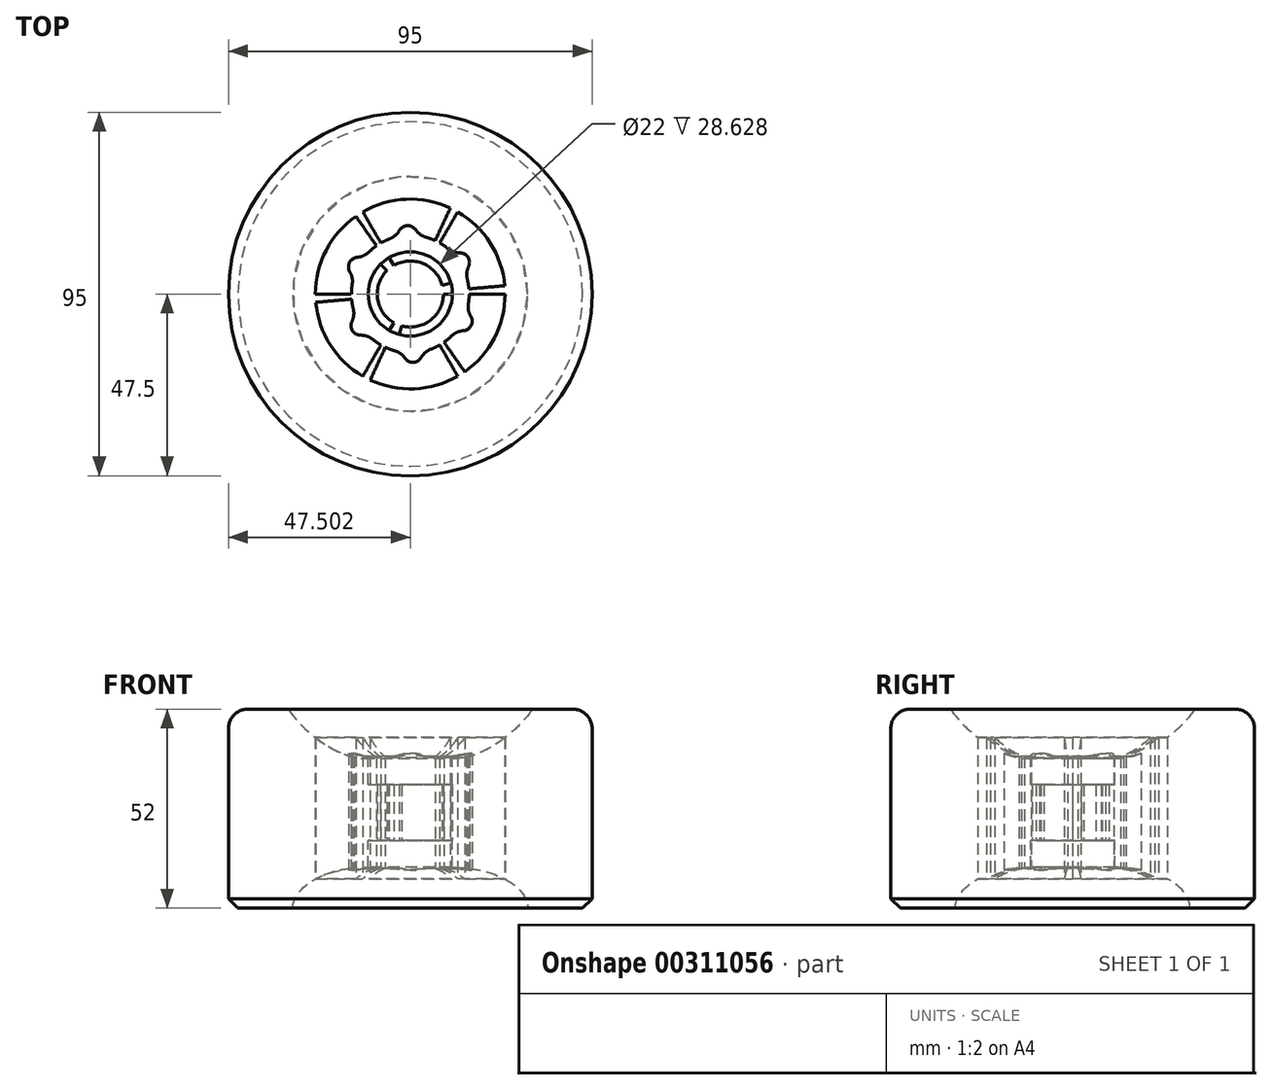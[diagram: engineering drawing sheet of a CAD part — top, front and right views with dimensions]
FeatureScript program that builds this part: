
annotation { "Feature Type Name" : "Feature", "Feature Type Description" : "" }
export const myFeature = defineFeature(function(context is Context, id is Id, definition is map)
    precondition{}
    {
        {
            var Q0;
            Q0=qCreatedBy(makeId("Front.planeOp"),FACE);
            var sketch = newSketch(context, id + "F0", { "sketchPlane" : qUnion([Q0])});
            skLineSegment(sketch, "E0", {"start": v(-20.2, 7.77) * mm, "end": v(-4.58, 7.77) * mm});
            skLineSegment(sketch, "E1", {"start": v(-20.2, 7.77) * mm, "end": v(-20.2, -18.23) * mm});
            skLineSegment(sketch, "E2", {"start": v(27.3, 7.77) * mm, "end": v(27.3, -18.23) * mm, "construction": true});
            skLineSegment(sketch, "E3", {"start": v(-20.2, -18.23) * mm, "end": v(-20.2, -44.23) * mm});
            skLineSegment(sketch, "E4", {"start": v(-20.2, -44.23) * mm, "end": v(-3.37, -44.23) * mm});
            skLineSegment(sketch, "E5", {"start": v(27.3, -18.23) * mm, "end": v(27.3, -44.23) * mm, "construction": true});
            skLineSegment(sketch, "E6", {"start": v(16.3, -4.93) * mm, "end": v(16.3, -33.56) * mm});
            skEllipticalArc(sketch, "E7", {});
            skEllipticalArc(sketch, "E8", {});
            const initialGuessF0  = {"E7": [0.006164850201457739, 0.0077684287428855915, -0.7508845168032906, 0.6604335261213568, 0.017096453369235928, 0.008044444951375029, 1.0795611750690233, 2.780946730637043], "E8": [0.016301685365613657, -0.04423157125711441, -1, 0, 0.01967554039205249, 0.010675819649360317, 4.71238898038469, 0]};
            skSetInitialGuess(sketch, initialGuessF0);
            skSolve(sketch);
        }
        {
            var Q0;
            Q0 = qSketchRegion(id + "F0", true);
            var Q1;
            Q1=sQuery(id+"F0.wireOp",EDGE,"E5");
            revolve(context, id + "F1", {"entities" : qUnion([Q0]), "axis" : qUnion([Q1]), "revolveType" : RevolveType.FULL});
        }
        {
            var Q0;
            Q0=makeQuery(id+"F1.opRevolve","SWEPT_EDGE",EDGE,{"disambiguationData":[OSD([sQuery(id+"F0.wireOp",EDGE,"E0"),sQuery(id+"F0.wireOp",EDGE,"E1")])]});
            fillet(context, id + "F2", {"entities" : qUnion([Q0]), "radius" : 5 * mm, "tangentPropagation" : true, "allowEdgeOverflow" : false});
        }
        {
            var Q0;
            Q0=makeQuery(id+"F1.opRevolve","SWEPT_EDGE",EDGE,{"disambiguationData":[OSD([sQuery(id+"F0.wireOp",EDGE,"E0"),sQuery(id+"F0.wireOp",EDGE,"E7")])]});
            fillet(context, id + "F3", {"entities" : qUnion([Q0]), "radius" : 1 * mm, "tangentPropagation" : true, "allowEdgeOverflow" : false});
        }
        {
            var Q0;
            Q0=makeQuery(id+"F1.opRevolve","SWEPT_FACE",FACE,{"disambiguationData":[OSD([sQuery(id+"F0.wireOp",EDGE,"E4")])]});
            var sketch = newSketch(context, id + "F4", { "sketchPlane" : qUnion([Q0])});
            skPoint(sketch, "E9.center", {"position": v(27.3, 0) * mm});
            skLineSegment(sketch, "E10.2.0", {"start": v(39.7, 21.46) * mm, "end": v(35, 13.32) * mm});
            skLineSegment(sketch, "E11.2.0", {"start": v(16.83, 22.46) * mm, "end": v(20.8, 13.94) * mm});
            skArc(sketch, "E12.trimOffspring", {"start": v(35, 13.32) * mm, "mid": v(33.88, 13.9) * mm, "end": v(32.73, 14.4) * mm});
            skArc(sketch, "E13.trimOffspring", {"start": v(39.7, 21.46) * mm, "mid": v(28.38, 24.76) * mm, "end": v(16.83, 22.46) * mm});
            skArc(sketch, "E14", {"start": v(30.15, 16.6) * mm, "mid": v(28.08, 17.87) * mm, "end": v(25.91, 16.8) * mm});
            skArc(sketch, "E15.trimOffspring", {"start": v(23.15, 14.81) * mm, "mid": v(21.96, 14.43) * mm, "end": v(20.8, 13.94) * mm});
            skArc(sketch, "E16.filletArc", {"start": v(23.15, 14.81) * mm, "mid": v(24.7, 15.56) * mm, "end": v(25.91, 16.8) * mm});
            skArc(sketch, "E17.filletArc", {"start": v(30.15, 16.6) * mm, "mid": v(31.25, 15.27) * mm, "end": v(32.73, 14.4) * mm});
            skLineSegment(sketch, "E18.1.0", {"start": v(14.9, 21.46) * mm, "end": v(19.6, 13.32) * mm});
            skLineSegment(sketch, "E18.1.1", {"start": v(2.61, 2.16) * mm, "end": v(11.97, 1.34) * mm});
            skArc(sketch, "E18.1.2", {"start": v(14.9, 21.46) * mm, "mid": v(6.4, 13.32) * mm, "end": v(2.61, 2.16) * mm});
            skArc(sketch, "E18.1.3", {"start": v(14.34, 10.77) * mm, "mid": v(16.05, 11.05) * mm, "end": v(17.55, 11.9) * mm});
            skArc(sketch, "E18.1.4", {"start": v(12.4, 3.81) * mm, "mid": v(12.13, 2.58) * mm, "end": v(11.97, 1.34) * mm});
            skArc(sketch, "E18.1.5", {"start": v(19.6, 13.32) * mm, "mid": v(18.55, 12.65) * mm, "end": v(17.55, 11.9) * mm});
            skArc(sketch, "E18.1.6", {"start": v(12.4, 3.81) * mm, "mid": v(12.53, 5.53) * mm, "end": v(12.07, 7.2) * mm});
            skArc(sketch, "E18.1.7", {"start": v(14.34, 10.77) * mm, "mid": v(12.22, 9.61) * mm, "end": v(12.07, 7.2) * mm});
            skLineSegment(sketch, "E18.2.0", {"start": v(2.52, 0) * mm, "end": v(11.92, 0) * mm});
            skLineSegment(sketch, "E18.2.1", {"start": v(13.09, -20.3) * mm, "end": v(18.48, -12.6) * mm});
            skArc(sketch, "E18.2.2", {"start": v(2.52, 0) * mm, "mid": v(5.32, -11.44) * mm, "end": v(13.09, -20.3) * mm});
            skArc(sketch, "E18.2.3", {"start": v(11.5, -5.84) * mm, "mid": v(12.1, -4.22) * mm, "end": v(12.12, -2.5) * mm});
            skArc(sketch, "E18.2.4", {"start": v(16.55, -11) * mm, "mid": v(17.48, -11.84) * mm, "end": v(18.48, -12.6) * mm});
            skArc(sketch, "E18.2.5", {"start": v(11.92, 0) * mm, "mid": v(11.97, -1.25) * mm, "end": v(12.12, -2.5) * mm});
            skArc(sketch, "E18.2.6", {"start": v(16.55, -11) * mm, "mid": v(15.12, -10.03) * mm, "end": v(13.45, -9.6) * mm});
            skArc(sketch, "E18.2.7", {"start": v(11.5, -5.84) * mm, "mid": v(11.44, -8.26) * mm, "end": v(13.45, -9.6) * mm});
            skLineSegment(sketch, "E18.3.0", {"start": v(14.9, -21.46) * mm, "end": v(19.6, -13.32) * mm});
            skLineSegment(sketch, "E18.3.1", {"start": v(37.78, -22.46) * mm, "end": v(33.8, -13.94) * mm});
            skArc(sketch, "E18.3.2", {"start": v(14.9, -21.46) * mm, "mid": v(26.22, -24.76) * mm, "end": v(37.78, -22.46) * mm});
            skArc(sketch, "E18.3.3", {"start": v(24.46, -16.6) * mm, "mid": v(23.36, -15.27) * mm, "end": v(21.87, -14.4) * mm});
            skArc(sketch, "E18.3.4", {"start": v(31.46, -14.81) * mm, "mid": v(32.65, -14.43) * mm, "end": v(33.8, -13.94) * mm});
            skArc(sketch, "E18.3.5", {"start": v(19.6, -13.32) * mm, "mid": v(20.72, -13.9) * mm, "end": v(21.87, -14.4) * mm});
            skArc(sketch, "E18.3.6", {"start": v(31.46, -14.81) * mm, "mid": v(29.9, -15.56) * mm, "end": v(28.69, -16.8) * mm});
            skArc(sketch, "E18.3.7", {"start": v(24.46, -16.6) * mm, "mid": v(26.52, -17.87) * mm, "end": v(28.69, -16.8) * mm});
            skLineSegment(sketch, "E18.4.0", {"start": v(39.7, -21.46) * mm, "end": v(35, -13.32) * mm});
            skLineSegment(sketch, "E18.4.1", {"start": v(52, -2.16) * mm, "end": v(42.63, -1.34) * mm});
            skArc(sketch, "E18.4.2", {"start": v(39.7, -21.46) * mm, "mid": v(48.2, -13.32) * mm, "end": v(52, -2.16) * mm});
            skArc(sketch, "E18.4.3", {"start": v(40.26, -10.77) * mm, "mid": v(38.56, -11.05) * mm, "end": v(37.05, -11.9) * mm});
            skArc(sketch, "E18.4.4", {"start": v(42.2, -3.81) * mm, "mid": v(42.47, -2.58) * mm, "end": v(42.63, -1.34) * mm});
            skArc(sketch, "E18.4.5", {"start": v(35, -13.32) * mm, "mid": v(36.05, -12.65) * mm, "end": v(37.05, -11.9) * mm});
            skArc(sketch, "E18.4.6", {"start": v(42.2, -3.81) * mm, "mid": v(42.08, -5.53) * mm, "end": v(42.54, -7.2) * mm});
            skArc(sketch, "E18.4.7", {"start": v(40.26, -10.77) * mm, "mid": v(42.39, -9.61) * mm, "end": v(42.54, -7.2) * mm});
            skLineSegment(sketch, "E18.5.0", {"start": v(52.09, 0) * mm, "end": v(42.69, 0) * mm});
            skLineSegment(sketch, "E18.5.1", {"start": v(41.52, 20.3) * mm, "end": v(36.13, 12.6) * mm});
            skArc(sketch, "E18.5.2", {"start": v(52.09, 0) * mm, "mid": v(49.29, 11.44) * mm, "end": v(41.52, 20.3) * mm});
            skArc(sketch, "E18.5.3", {"start": v(43.1, 5.84) * mm, "mid": v(42.5, 4.22) * mm, "end": v(42.48, 2.5) * mm});
            skArc(sketch, "E18.5.4", {"start": v(38.05, 11) * mm, "mid": v(37.12, 11.84) * mm, "end": v(36.13, 12.6) * mm});
            skArc(sketch, "E18.5.5", {"start": v(42.69, 0) * mm, "mid": v(42.64, 1.25) * mm, "end": v(42.48, 2.5) * mm});
            skArc(sketch, "E18.5.6", {"start": v(38.05, 11) * mm, "mid": v(39.48, 10.03) * mm, "end": v(41.15, 9.6) * mm});
            skArc(sketch, "E18.5.7", {"start": v(43.1, 5.84) * mm, "mid": v(43.17, 8.26) * mm, "end": v(41.15, 9.6) * mm});
            skSolve(sketch);
        }
        {
            var Q0;
            Q0 = qSketchRegion(id + "F4", true);
            extrude(context, id + "F5", {"entities" : qUnion([Q0]), "operationType" : NewBodyOperationType.REMOVE, "oppositeDirection" : true, "depth" : 137.1 * mm});
        }
        {
            var Q0;
            Q0=makeQuery(id+"F1.opRevolve","SWEPT_EDGE",EDGE,{"disambiguationData":[OSD([sQuery(id+"F0.wireOp",EDGE,"E3"),sQuery(id+"F0.wireOp",EDGE,"E4")])]});
            chamfer(context, id + "F6", {"entities" : qUnion([Q0]), "width" : 2.5 * mm, "tangentPropagation" : true});
        }
        {
            var Q0;
            Q0=makeQuery(id+"F1.opRevolve","SWEPT_FACE",FACE,{"disambiguationData":[OSD([sQuery(id+"F0.wireOp",EDGE,"E4")])]});
            var sketch = newSketch(context, id + "F7", { "sketchPlane" : qUnion([Q0])});
            skCircle(sketch, "E19", {"center": v(27.3, 0) * mm, "radius": 11 * mm});
            skLineSegment(sketch, "E20", {"start": v(35.94, 0) * mm, "end": v(38.3, 0) * mm});
            skLineSegment(sketch, "E21.2.0", {"start": v(35.64, -2.24) * mm, "end": v(37.93, -2.85) * mm});
            skLineSegment(sketch, "E22.1.0", {"start": v(21.2, -6.1) * mm, "end": v(19.52, -7.78) * mm});
            skLineSegment(sketch, "E22.1.1", {"start": v(22.98, -7.48) * mm, "end": v(21.8, -9.53) * mm});
            skLineSegment(sketch, "E22.2.0", {"start": v(25.07, 8.34) * mm, "end": v(24.45, 10.63) * mm});
            skLineSegment(sketch, "E22.2.1", {"start": v(22.98, 7.48) * mm, "end": v(21.8, 9.53) * mm});
            skCircle(sketch, "E23", {"center": v(27.3, 0) * mm, "radius": 8.64 * mm});
            skSolve(sketch);
        }
        {
            var Q0;
            Q0 = qSketchRegion(id + "F7", true);
            extrude(context, id + "F8", {"entities" : qUnion([Q0]), "operationType" : NewBodyOperationType.ADD, "oppositeDirection" : true, "depth" : 32.3 * mm, "hasSecondDirection" : true, "secondDirectionOppositeDirection" : false, "secondDirectionDepth" : -17.7 * mm});
        }
        {
            var Q0;
            {var subQ0=sQuery(id+"F7.wireOp",EDGE,"E22.2.0");Q0=makeQuery(id+"F7.imprint","IMPRINT",FACE,{"disambiguationData":[TD([[makeQuery(id+"F7.imprint","IMPRINT",EDGE,{"derivedFrom":subQ0}),1.0]])]});}
            var Q1;
            {var subQ0=sQuery(id+"F7.wireOp",EDGE,"E22.1.0");Q1=makeQuery(id+"F7.imprint","IMPRINT",FACE,{"disambiguationData":[TD([[makeQuery(id+"F7.imprint","IMPRINT",EDGE,{"derivedFrom":subQ0}),1.0]])]});}
            var Q2;
            {var subQ0=sQuery(id+"F7.wireOp",EDGE,"E20");Q2=makeQuery(id+"F7.imprint","IMPRINT",FACE,{"disambiguationData":[TD([[makeQuery(id+"F7.imprint","IMPRINT",EDGE,{"derivedFrom":subQ0}),-1.0]])]});}
            extrude(context, id + "F9", {"entities" : qUnion([Q0, Q1, Q2]), "operationType" : NewBodyOperationType.REMOVE, "oppositeDirection" : true, "depth" : 48.5 * mm});
        }
    });
